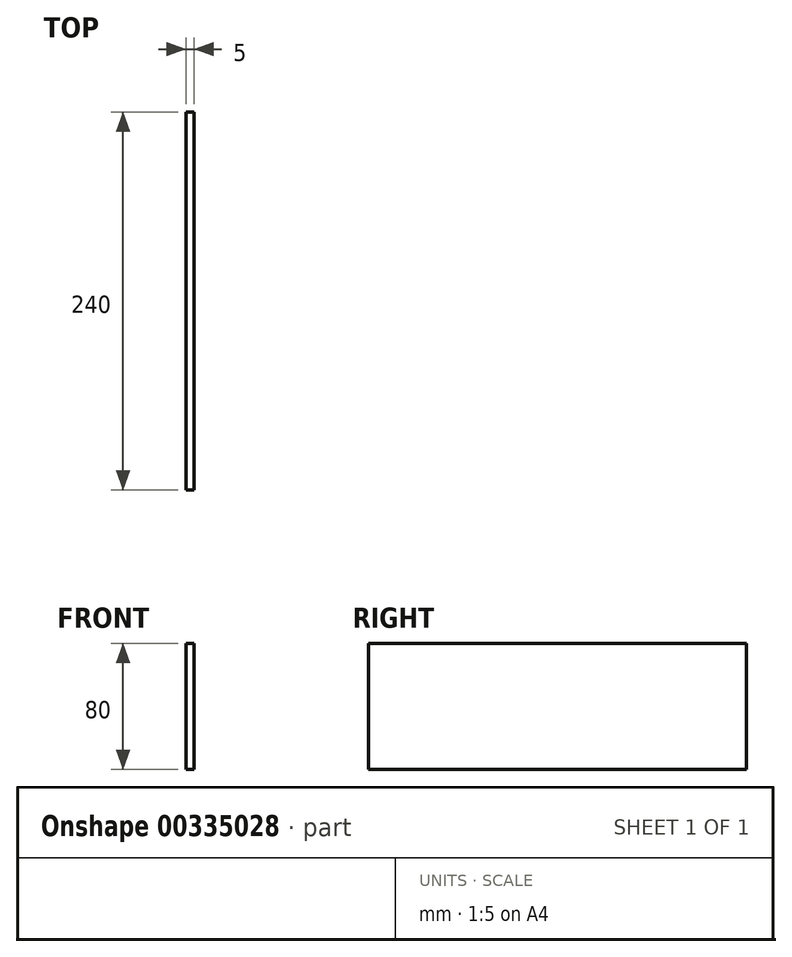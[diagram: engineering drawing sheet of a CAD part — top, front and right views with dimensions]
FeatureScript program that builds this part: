
annotation { "Feature Type Name" : "Feature", "Feature Type Description" : "" }
export const myFeature = defineFeature(function(context is Context, id is Id, definition is map)
    precondition{}
    {
        {
            var Q0;
            Q0=qCreatedBy(makeId("Top.planeOp"),FACE);
            var sketch = newSketch(context, id + "F0", { "sketchPlane" : qUnion([Q0])});
            skLineSegment(sketch, "E0.bottom", {"start": v(2.5, -120) * mm, "end": v(-2.5, -120) * mm});
            skLineSegment(sketch, "E0.top", {"start": v(2.5, 120) * mm, "end": v(-2.5, 120) * mm});
            skLineSegment(sketch, "E0.left", {"start": v(2.5, -120) * mm, "end": v(2.5, 120) * mm});
            skLineSegment(sketch, "E0.right", {"start": v(-2.5, -120) * mm, "end": v(-2.5, 120) * mm});
            skPoint(sketch, "E0.middle", {"position": v(0, 0) * mm});
            skSolve(sketch);
        }
        {
            var Q0;
            Q0 = qSketchRegion(id + "F0", true);
            extrude(context, id + "F1", {"entities" : qUnion([Q0]), "depth" : 80 * mm});
        }
    });
